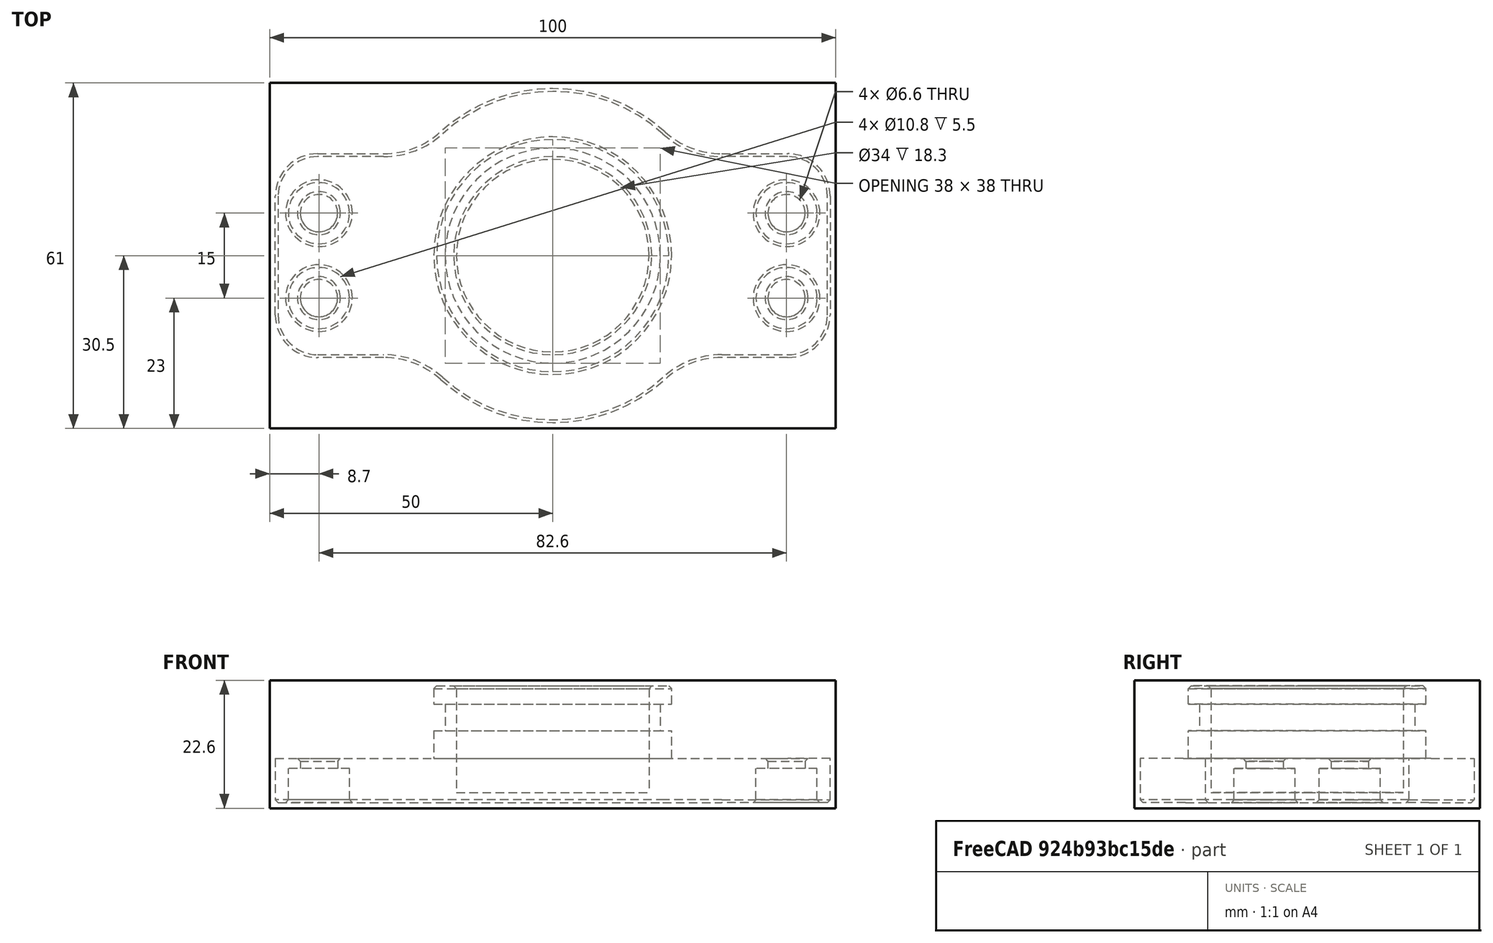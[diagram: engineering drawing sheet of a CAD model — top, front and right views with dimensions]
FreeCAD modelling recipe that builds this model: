
FCSTD DOCUMENT  (FreeCAD 0.18R15914 +62 (Git))
Label: DizzyBlank
License: All rights reserved
LicenseURL: http://en.wikipedia.org/wiki/All_rights_reserved
objects: Path::FeaturePython×3, Part::FeaturePython×2, Part::Feature×1, App::FeaturePython×1, App::DocumentObjectGroup×1, Path::FeatureCompoundPython×1
note: 3 computed .brp shape members not serialized (recipe doc carries the construction recipe); baked Part::Feature solids carry a one-line shape summary decoded from their .brp

FEATURE [Part::Feature] Part__Feature  label="Distributor Blanking Plate VW 9A/KR v15 v1"
  Placement = pos=(0,0,0) rot=(-1,0,0;1.5708rad)
  shape: bbox 98 x 59 x 20.6 mm, 64 faces (baked)
FEATURE [App::FeaturePython] SetupSheet  # Path/CAM operation (typed FeaturePython)
  ClearanceHeightExpression = OpStockZMax+SetupSheet.ClearanceHeightOffset
  ClearanceHeightOffset = 5
  FinalDepthExpression = OpFinalDepth
  HorizRapid = 0
  SafeHeightExpression = OpStockZMax+SetupSheet.SafeHeightOffset
  SafeHeightOffset = 3
  StartDepthExpression = OpStartDepth
  StepDownExpression = OpToolDiameter
  VertRapid = 0
FEATURE [Part::FeaturePython] Clone  label="Model-Distributor Blanking Plate VW 9A/KR v15 v1"  # Draft clone (typed FeaturePython)
  AttacherType = Attacher::AttachEngine3D
  Fuse = false
  Objects = -> [Part__Feature]
  PathResource = Model
  Placement = pos=(1,60,8.8) rot=(-1,0,0;1.5708rad)
  Scale = (1,1,1)
FEATURE [App::DocumentObjectGroup] Model
  Group = -> [Clone]
FEATURE [Path::FeaturePython] Default_Tool  label="Default Tool"  # Path/CAM operation (typed FeaturePython)
  HorizFeed = 0
  HorizRapid = 0
  SpindleDir = 0
  SpindleSpeed = 0
  ToolNumber = 1
  VertFeed = 0
  VertRapid = 0
  expr: HorizRapid = SetupSheet.HorizRapid
  expr: VertRapid = SetupSheet.VertRapid
FEATURE [Part::FeaturePython] Stock  # WARN: FeaturePython — macro-defined, semantics opaque (R4)
  Base = -> Model
  ExtXneg = 1
  ExtXpos = 1
  ExtYneg = 1
  ExtYpos = 1
  ExtZneg = 1
  ExtZpos = 1
  Placement = pos=(1,1,1) rot=(0,0,1;0rad)
  StockType = FromBase
FEATURE [Path::FeaturePython] Surface  # Path/CAM operation (typed FeaturePython)
  Active = true
  Algorithm = 0
  BoundBox = 0
  ClearanceHeight = 27.6
  DepthOffset = 0
  DropCutterDir = 0
  DropCutterExtraOffset = (0,0,0)
  FinalDepth = 2
  OpFinalDepth = 21.6
  OpStartDepth = 22.6
  OpStockZMax = 22.6
  OpStockZMin = 0
  OpToolDiameter = 5
  Optimize = true
  SafeHeight = 25.6
  SampleInterval = 0.05
  StartDepth = 22.6
  StepDown = 5
  StepOver = 50
  ToolController = -> Default_Tool
  expr: ClearanceHeight = OpStockZMax + SetupSheet.ClearanceHeightOffset
  expr: SafeHeight = OpStockZMax + SetupSheet.SafeHeightOffset
  expr: StepDown = OpToolDiameter
  expr: StartDepth = OpStartDepth
FEATURE [Path::FeatureCompoundPython] Operations  # Path/CAM operation (typed FeaturePython)
  Group = -> [Surface]
  UsePlacements = false
FEATURE [Path::FeaturePython] Job  # Path/CAM operation (typed FeaturePython)
  GeometryTolerance = 0.1
  Model = -> Model
  Operations = -> Operations
  PostProcessor = 1
  SetupSheet = -> SetupSheet
  Stock = -> Stock
  ToolController = -> [Default_Tool]
